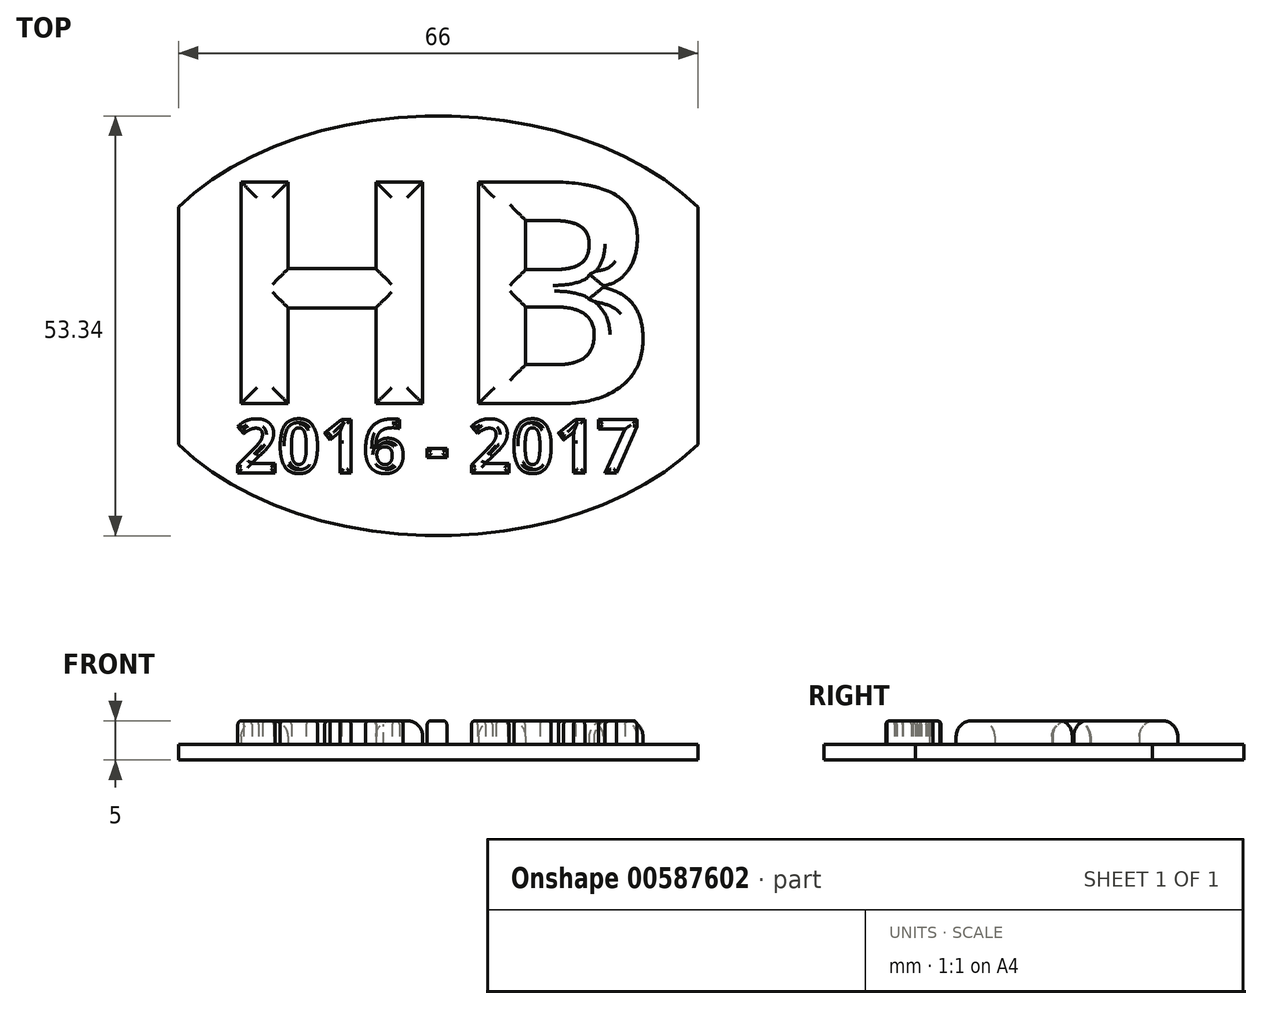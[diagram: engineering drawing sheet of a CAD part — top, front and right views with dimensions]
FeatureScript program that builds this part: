
annotation { "Feature Type Name" : "Feature", "Feature Type Description" : "" }
export const myFeature = defineFeature(function(context is Context, id is Id, definition is map)
    precondition{}
    {
        {
            var Q0;
            Q0=qCreatedBy(makeId("Top.planeOp"),FACE);
            var sketch = newSketch(context, id + "F0", { "sketchPlane" : qUnion([Q0])});
            skEllipse(sketch, "E0", {"center": v(0, 0) * mm, "majorRadius": 40 * mm, "minorRadius": 26.67 * mm, "majorAxis": v(1, 0)});
            skLineSegment(sketch, "E1", {"start": v(-33, 15.07) * mm, "end": v(-33, -15.07) * mm});
            skLineSegment(sketch, "E2", {"start": v(0, 26.67) * mm, "end": v(0, -26.67) * mm, "construction": true});
            skLineSegment(sketch, "E3.MirrorCS", {"start": v(33, 15.07) * mm, "end": v(33, -15.07) * mm});
            skText(sketch, "E4", { "text": "HB", "fontName": "OpenSans-Bold.ttf"});
            skText(sketch, "E5", { "text": "2016 - 2017\n", "fontName": "OpenSans-Bold.ttf"});
            const initialGuessF0  = {"E4": [-0.02857, -0.00987, 1, 0, 0.02839], "E5": [-0.02583, -0.01869, 1, 0, 0.00684]};
            skSetInitialGuess(sketch, initialGuessF0);
            skSolve(sketch);
        }
        {
            var Q0;
            {var subQ0=sQuery(id+"F0.wireOp",EDGE,"E1");Q0=makeQuery(id+"F0.imprint","IMPRINT",FACE,{"disambiguationData":[TD([[makeQuery(id+"F0.imprint","IMPRINT",EDGE,{"derivedFrom":subQ0}),1.0]])]});}
            var Q1;
            Q1=makeQuery(id+"F0.imprint","IMPRINT",FACE,{"disambiguationData":[TD([[makeQuery(id+"F0.imprint","IMPRINT",EDGE,{"derivedFrom":sQuery(id+"F0.wireOp",EDGE,"E4.sketch_text.stroke-31")}),1.0]])]});
            var Q2;
            Q2=makeQuery(id+"F0.imprint","IMPRINT",FACE,{"disambiguationData":[TD([[makeQuery(id+"F0.imprint","IMPRINT",EDGE,{"derivedFrom":sQuery(id+"F0.wireOp",EDGE,"E4.sketch_text.stroke-24")}),1.0]])]});
            var Q3;
            Q3=makeQuery(id+"F0.imprint","IMPRINT",FACE,{"disambiguationData":[TD([[makeQuery(id+"F0.imprint","IMPRINT",EDGE,{"derivedFrom":sQuery(id+"F0.wireOp",EDGE,"E5.sketch_text.stroke-111")}),1.0]])]});
            var Q4;
            Q4=makeQuery(id+"F0.imprint","IMPRINT",FACE,{"disambiguationData":[TD([[makeQuery(id+"F0.imprint","IMPRINT",EDGE,{"derivedFrom":sQuery(id+"F0.wireOp",EDGE,"E5.sketch_text.stroke-67")}),1.0]])]});
            var Q5;
            Q5=makeQuery(id+"F0.imprint","IMPRINT",FACE,{"disambiguationData":[TD([[makeQuery(id+"F0.imprint","IMPRINT",EDGE,{"derivedFrom":sQuery(id+"F0.wireOp",EDGE,"E5.sketch_text.stroke-32")}),1.0]])]});
            extrude(context, id + "F1", {"entities" : qUnion([Q0, Q1, Q2, Q3, Q4, Q5]), "depth" : 2 * mm, "offsetDistance" : 25 * mm});
        }
        {
            var Q0;
            Q0=makeQuery(id+"F0.imprint","IMPRINT",FACE,{"disambiguationData":[TD([[makeQuery(id+"F0.imprint","IMPRINT",EDGE,{"derivedFrom":sQuery(id+"F0.wireOp",EDGE,"E4.sketch_text.stroke-0")}),-1.0]])]});
            var Q1;
            Q1=makeQuery(id+"F0.imprint","IMPRINT",FACE,{"disambiguationData":[TD([[makeQuery(id+"F0.imprint","IMPRINT",EDGE,{"derivedFrom":sQuery(id+"F0.wireOp",EDGE,"E4.sketch_text.stroke-12")}),-1.0]])]});
            var Q2;
            Q2=makeQuery(id+"F0.imprint","IMPRINT",FACE,{"disambiguationData":[TD([[makeQuery(id+"F0.imprint","IMPRINT",EDGE,{"derivedFrom":sQuery(id+"F0.wireOp",EDGE,"E5.sketch_text.stroke-40")}),-1.0]])]});
            var Q3;
            Q3=makeQuery(id+"F0.imprint","IMPRINT",FACE,{"disambiguationData":[TD([[makeQuery(id+"F0.imprint","IMPRINT",EDGE,{"derivedFrom":sQuery(id+"F0.wireOp",EDGE,"E5.sketch_text.stroke-50")}),-1.0]])]});
            var Q4;
            Q4=makeQuery(id+"F0.imprint","IMPRINT",FACE,{"disambiguationData":[TD([[makeQuery(id+"F0.imprint","IMPRINT",EDGE,{"derivedFrom":sQuery(id+"F0.wireOp",EDGE,"E5.sketch_text.stroke-24")}),-1.0]])]});
            var Q5;
            Q5=makeQuery(id+"F0.imprint","IMPRINT",FACE,{"disambiguationData":[TD([[makeQuery(id+"F0.imprint","IMPRINT",EDGE,{"derivedFrom":sQuery(id+"F0.wireOp",EDGE,"E5.sketch_text.stroke-75")}),-1.0]])]});
            var Q6;
            Q6=makeQuery(id+"F0.imprint","IMPRINT",FACE,{"disambiguationData":[TD([[makeQuery(id+"F0.imprint","IMPRINT",EDGE,{"derivedFrom":sQuery(id+"F0.wireOp",EDGE,"E5.sketch_text.stroke-79")}),-1.0]])]});
            var Q7;
            Q7=makeQuery(id+"F0.imprint","IMPRINT",FACE,{"disambiguationData":[TD([[makeQuery(id+"F0.imprint","IMPRINT",EDGE,{"derivedFrom":sQuery(id+"F0.wireOp",EDGE,"E5.sketch_text.stroke-103")}),-1.0]])]});
            var Q8;
            Q8=makeQuery(id+"F0.imprint","IMPRINT",FACE,{"disambiguationData":[TD([[makeQuery(id+"F0.imprint","IMPRINT",EDGE,{"derivedFrom":sQuery(id+"F0.wireOp",EDGE,"E5.sketch_text.stroke-119")}),-1.0]])]});
            var Q9;
            Q9=makeQuery(id+"F0.imprint","IMPRINT",FACE,{"disambiguationData":[TD([[makeQuery(id+"F0.imprint","IMPRINT",EDGE,{"derivedFrom":sQuery(id+"F0.wireOp",EDGE,"E5.sketch_text.stroke-129")}),-1.0]])]});
            var Q10;
            Q10=makeQuery(id+"F0.imprint","IMPRINT",FACE,{"disambiguationData":[TD([[makeQuery(id+"F0.imprint","IMPRINT",EDGE,{"derivedFrom":sQuery(id+"F0.wireOp",EDGE,"E5.sketch_text.stroke-0")}),-1.0]])]});
            extrude(context, id + "F2", {"entities" : qUnion([Q0, Q1, Q2, Q3, Q4, Q5, Q6, Q7, Q8, Q9, Q10]), "operationType" : NewBodyOperationType.ADD, "depth" : 5 * mm, "offsetDistance" : 25 * mm});
        }
        {
            var Q0;
            Q0=makeQuery(id+"F2.opExtrude","CAP_FACE",FACE,{"disambiguationData":[OSD([sQuery(id+"F0.wireOp",EDGE,"E4.sketch_text.stroke-0"),sQuery(id+"F0.wireOp",EDGE,"E4.sketch_text.stroke-1"),sQuery(id+"F0.wireOp",EDGE,"E4.sketch_text.stroke-2"),sQuery(id+"F0.wireOp",EDGE,"E4.sketch_text.stroke-3"),sQuery(id+"F0.wireOp",EDGE,"E4.sketch_text.stroke-4"),sQuery(id+"F0.wireOp",EDGE,"E4.sketch_text.stroke-5"),sQuery(id+"F0.wireOp",EDGE,"E4.sketch_text.stroke-6"),sQuery(id+"F0.wireOp",EDGE,"E4.sketch_text.stroke-7"),sQuery(id+"F0.wireOp",EDGE,"E4.sketch_text.stroke-8"),sQuery(id+"F0.wireOp",EDGE,"E4.sketch_text.stroke-9"),sQuery(id+"F0.wireOp",EDGE,"E4.sketch_text.stroke-10"),sQuery(id+"F0.wireOp",EDGE,"E4.sketch_text.stroke-11")])],"isStart":false});
            var Q1;
            Q1=makeQuery(id+"F2.opExtrude","CAP_FACE",FACE,{"disambiguationData":[OSD([sQuery(id+"F0.wireOp",EDGE,"E4.sketch_text.stroke-12"),sQuery(id+"F0.wireOp",EDGE,"E4.sketch_text.stroke-13"),sQuery(id+"F0.wireOp",EDGE,"E4.sketch_text.stroke-14"),sQuery(id+"F0.wireOp",EDGE,"E4.sketch_text.stroke-15"),sQuery(id+"F0.wireOp",EDGE,"E4.sketch_text.stroke-16"),sQuery(id+"F0.wireOp",EDGE,"E4.sketch_text.stroke-17"),sQuery(id+"F0.wireOp",EDGE,"E4.sketch_text.stroke-18"),sQuery(id+"F0.wireOp",EDGE,"E4.sketch_text.stroke-19"),sQuery(id+"F0.wireOp",EDGE,"E4.sketch_text.stroke-20"),sQuery(id+"F0.wireOp",EDGE,"E4.sketch_text.stroke-21"),sQuery(id+"F0.wireOp",EDGE,"E4.sketch_text.stroke-22"),sQuery(id+"F0.wireOp",EDGE,"E4.sketch_text.stroke-23"),sQuery(id+"F0.wireOp",EDGE,"E4.sketch_text.stroke-24"),sQuery(id+"F0.wireOp",EDGE,"E4.sketch_text.stroke-25"),sQuery(id+"F0.wireOp",EDGE,"E4.sketch_text.stroke-26"),sQuery(id+"F0.wireOp",EDGE,"E4.sketch_text.stroke-27"),sQuery(id+"F0.wireOp",EDGE,"E4.sketch_text.stroke-28"),sQuery(id+"F0.wireOp",EDGE,"E4.sketch_text.stroke-29"),sQuery(id+"F0.wireOp",EDGE,"E4.sketch_text.stroke-30"),sQuery(id+"F0.wireOp",EDGE,"E4.sketch_text.stroke-31"),sQuery(id+"F0.wireOp",EDGE,"E4.sketch_text.stroke-32"),sQuery(id+"F0.wireOp",EDGE,"E4.sketch_text.stroke-33"),sQuery(id+"F0.wireOp",EDGE,"E4.sketch_text.stroke-34"),sQuery(id+"F0.wireOp",EDGE,"E4.sketch_text.stroke-35"),sQuery(id+"F0.wireOp",EDGE,"E4.sketch_text.stroke-36")])],"isStart":false});
            fillet(context, id + "F3", {"entities" : qUnion([Q0, Q1]), "radius" : 2 * mm, "tangentPropagation" : true, "allowEdgeOverflow" : false});
        }
        {
            var Q0;
            Q0=makeQuery(id+"F2.opExtrude","CAP_FACE",FACE,{"disambiguationData":[OSD([sQuery(id+"F0.wireOp",EDGE,"E5.sketch_text.stroke-0"),sQuery(id+"F0.wireOp",EDGE,"E5.sketch_text.stroke-1"),sQuery(id+"F0.wireOp",EDGE,"E5.sketch_text.stroke-2"),sQuery(id+"F0.wireOp",EDGE,"E5.sketch_text.stroke-3"),sQuery(id+"F0.wireOp",EDGE,"E5.sketch_text.stroke-4"),sQuery(id+"F0.wireOp",EDGE,"E5.sketch_text.stroke-5"),sQuery(id+"F0.wireOp",EDGE,"E5.sketch_text.stroke-6"),sQuery(id+"F0.wireOp",EDGE,"E5.sketch_text.stroke-7"),sQuery(id+"F0.wireOp",EDGE,"E5.sketch_text.stroke-8"),sQuery(id+"F0.wireOp",EDGE,"E5.sketch_text.stroke-9"),sQuery(id+"F0.wireOp",EDGE,"E5.sketch_text.stroke-10"),sQuery(id+"F0.wireOp",EDGE,"E5.sketch_text.stroke-11"),sQuery(id+"F0.wireOp",EDGE,"E5.sketch_text.stroke-12"),sQuery(id+"F0.wireOp",EDGE,"E5.sketch_text.stroke-13"),sQuery(id+"F0.wireOp",EDGE,"E5.sketch_text.stroke-14"),sQuery(id+"F0.wireOp",EDGE,"E5.sketch_text.stroke-15"),sQuery(id+"F0.wireOp",EDGE,"E5.sketch_text.stroke-16"),sQuery(id+"F0.wireOp",EDGE,"E5.sketch_text.stroke-17"),sQuery(id+"F0.wireOp",EDGE,"E5.sketch_text.stroke-18"),sQuery(id+"F0.wireOp",EDGE,"E5.sketch_text.stroke-19"),sQuery(id+"F0.wireOp",EDGE,"E5.sketch_text.stroke-20"),sQuery(id+"F0.wireOp",EDGE,"E5.sketch_text.stroke-21"),sQuery(id+"F0.wireOp",EDGE,"E5.sketch_text.stroke-22"),sQuery(id+"F0.wireOp",EDGE,"E5.sketch_text.stroke-23")])],"isStart":false});
            var Q1;
            Q1=makeQuery(id+"F2.opExtrude","CAP_FACE",FACE,{"disambiguationData":[OSD([sQuery(id+"F0.wireOp",EDGE,"E5.sketch_text.stroke-24"),sQuery(id+"F0.wireOp",EDGE,"E5.sketch_text.stroke-25"),sQuery(id+"F0.wireOp",EDGE,"E5.sketch_text.stroke-26"),sQuery(id+"F0.wireOp",EDGE,"E5.sketch_text.stroke-27"),sQuery(id+"F0.wireOp",EDGE,"E5.sketch_text.stroke-28"),sQuery(id+"F0.wireOp",EDGE,"E5.sketch_text.stroke-29"),sQuery(id+"F0.wireOp",EDGE,"E5.sketch_text.stroke-30"),sQuery(id+"F0.wireOp",EDGE,"E5.sketch_text.stroke-31"),sQuery(id+"F0.wireOp",EDGE,"E5.sketch_text.stroke-32"),sQuery(id+"F0.wireOp",EDGE,"E5.sketch_text.stroke-33"),sQuery(id+"F0.wireOp",EDGE,"E5.sketch_text.stroke-34"),sQuery(id+"F0.wireOp",EDGE,"E5.sketch_text.stroke-35"),sQuery(id+"F0.wireOp",EDGE,"E5.sketch_text.stroke-36"),sQuery(id+"F0.wireOp",EDGE,"E5.sketch_text.stroke-37"),sQuery(id+"F0.wireOp",EDGE,"E5.sketch_text.stroke-38"),sQuery(id+"F0.wireOp",EDGE,"E5.sketch_text.stroke-39")])],"isStart":false});
            var Q2;
            Q2=makeQuery(id+"F2.opExtrude","CAP_FACE",FACE,{"disambiguationData":[OSD([sQuery(id+"F0.wireOp",EDGE,"E5.sketch_text.stroke-40"),sQuery(id+"F0.wireOp",EDGE,"E5.sketch_text.stroke-41"),sQuery(id+"F0.wireOp",EDGE,"E5.sketch_text.stroke-42"),sQuery(id+"F0.wireOp",EDGE,"E5.sketch_text.stroke-43"),sQuery(id+"F0.wireOp",EDGE,"E5.sketch_text.stroke-44"),sQuery(id+"F0.wireOp",EDGE,"E5.sketch_text.stroke-45"),sQuery(id+"F0.wireOp",EDGE,"E5.sketch_text.stroke-46"),sQuery(id+"F0.wireOp",EDGE,"E5.sketch_text.stroke-47"),sQuery(id+"F0.wireOp",EDGE,"E5.sketch_text.stroke-48"),sQuery(id+"F0.wireOp",EDGE,"E5.sketch_text.stroke-49")])],"isStart":false});
            var Q3;
            Q3=makeQuery(id+"F2.opExtrude","CAP_FACE",FACE,{"disambiguationData":[OSD([sQuery(id+"F0.wireOp",EDGE,"E5.sketch_text.stroke-50"),sQuery(id+"F0.wireOp",EDGE,"E5.sketch_text.stroke-51"),sQuery(id+"F0.wireOp",EDGE,"E5.sketch_text.stroke-52"),sQuery(id+"F0.wireOp",EDGE,"E5.sketch_text.stroke-53"),sQuery(id+"F0.wireOp",EDGE,"E5.sketch_text.stroke-54"),sQuery(id+"F0.wireOp",EDGE,"E5.sketch_text.stroke-55"),sQuery(id+"F0.wireOp",EDGE,"E5.sketch_text.stroke-56"),sQuery(id+"F0.wireOp",EDGE,"E5.sketch_text.stroke-57"),sQuery(id+"F0.wireOp",EDGE,"E5.sketch_text.stroke-58"),sQuery(id+"F0.wireOp",EDGE,"E5.sketch_text.stroke-59"),sQuery(id+"F0.wireOp",EDGE,"E5.sketch_text.stroke-60"),sQuery(id+"F0.wireOp",EDGE,"E5.sketch_text.stroke-61"),sQuery(id+"F0.wireOp",EDGE,"E5.sketch_text.stroke-62"),sQuery(id+"F0.wireOp",EDGE,"E5.sketch_text.stroke-63"),sQuery(id+"F0.wireOp",EDGE,"E5.sketch_text.stroke-64"),sQuery(id+"F0.wireOp",EDGE,"E5.sketch_text.stroke-65"),sQuery(id+"F0.wireOp",EDGE,"E5.sketch_text.stroke-66"),sQuery(id+"F0.wireOp",EDGE,"E5.sketch_text.stroke-67"),sQuery(id+"F0.wireOp",EDGE,"E5.sketch_text.stroke-68"),sQuery(id+"F0.wireOp",EDGE,"E5.sketch_text.stroke-69"),sQuery(id+"F0.wireOp",EDGE,"E5.sketch_text.stroke-70"),sQuery(id+"F0.wireOp",EDGE,"E5.sketch_text.stroke-71"),sQuery(id+"F0.wireOp",EDGE,"E5.sketch_text.stroke-72"),sQuery(id+"F0.wireOp",EDGE,"E5.sketch_text.stroke-73"),sQuery(id+"F0.wireOp",EDGE,"E5.sketch_text.stroke-74")])],"isStart":false});
            var Q4;
            Q4=makeQuery(id+"F2.opExtrude","CAP_FACE",FACE,{"disambiguationData":[OSD([sQuery(id+"F0.wireOp",EDGE,"E5.sketch_text.stroke-75"),sQuery(id+"F0.wireOp",EDGE,"E5.sketch_text.stroke-76"),sQuery(id+"F0.wireOp",EDGE,"E5.sketch_text.stroke-77"),sQuery(id+"F0.wireOp",EDGE,"E5.sketch_text.stroke-78")])],"isStart":false});
            var Q5;
            Q5=makeQuery(id+"F2.opExtrude","CAP_FACE",FACE,{"disambiguationData":[OSD([sQuery(id+"F0.wireOp",EDGE,"E5.sketch_text.stroke-79"),sQuery(id+"F0.wireOp",EDGE,"E5.sketch_text.stroke-80"),sQuery(id+"F0.wireOp",EDGE,"E5.sketch_text.stroke-81"),sQuery(id+"F0.wireOp",EDGE,"E5.sketch_text.stroke-82"),sQuery(id+"F0.wireOp",EDGE,"E5.sketch_text.stroke-83"),sQuery(id+"F0.wireOp",EDGE,"E5.sketch_text.stroke-84"),sQuery(id+"F0.wireOp",EDGE,"E5.sketch_text.stroke-85"),sQuery(id+"F0.wireOp",EDGE,"E5.sketch_text.stroke-86"),sQuery(id+"F0.wireOp",EDGE,"E5.sketch_text.stroke-87"),sQuery(id+"F0.wireOp",EDGE,"E5.sketch_text.stroke-88"),sQuery(id+"F0.wireOp",EDGE,"E5.sketch_text.stroke-89"),sQuery(id+"F0.wireOp",EDGE,"E5.sketch_text.stroke-90"),sQuery(id+"F0.wireOp",EDGE,"E5.sketch_text.stroke-91"),sQuery(id+"F0.wireOp",EDGE,"E5.sketch_text.stroke-92"),sQuery(id+"F0.wireOp",EDGE,"E5.sketch_text.stroke-93"),sQuery(id+"F0.wireOp",EDGE,"E5.sketch_text.stroke-94"),sQuery(id+"F0.wireOp",EDGE,"E5.sketch_text.stroke-95"),sQuery(id+"F0.wireOp",EDGE,"E5.sketch_text.stroke-96"),sQuery(id+"F0.wireOp",EDGE,"E5.sketch_text.stroke-97"),sQuery(id+"F0.wireOp",EDGE,"E5.sketch_text.stroke-98"),sQuery(id+"F0.wireOp",EDGE,"E5.sketch_text.stroke-99"),sQuery(id+"F0.wireOp",EDGE,"E5.sketch_text.stroke-100"),sQuery(id+"F0.wireOp",EDGE,"E5.sketch_text.stroke-101"),sQuery(id+"F0.wireOp",EDGE,"E5.sketch_text.stroke-102")])],"isStart":false});
            var Q6;
            Q6=makeQuery(id+"F2.opExtrude","CAP_FACE",FACE,{"disambiguationData":[OSD([sQuery(id+"F0.wireOp",EDGE,"E5.sketch_text.stroke-103"),sQuery(id+"F0.wireOp",EDGE,"E5.sketch_text.stroke-104"),sQuery(id+"F0.wireOp",EDGE,"E5.sketch_text.stroke-105"),sQuery(id+"F0.wireOp",EDGE,"E5.sketch_text.stroke-106"),sQuery(id+"F0.wireOp",EDGE,"E5.sketch_text.stroke-107"),sQuery(id+"F0.wireOp",EDGE,"E5.sketch_text.stroke-108"),sQuery(id+"F0.wireOp",EDGE,"E5.sketch_text.stroke-109"),sQuery(id+"F0.wireOp",EDGE,"E5.sketch_text.stroke-110"),sQuery(id+"F0.wireOp",EDGE,"E5.sketch_text.stroke-111"),sQuery(id+"F0.wireOp",EDGE,"E5.sketch_text.stroke-112"),sQuery(id+"F0.wireOp",EDGE,"E5.sketch_text.stroke-113"),sQuery(id+"F0.wireOp",EDGE,"E5.sketch_text.stroke-114"),sQuery(id+"F0.wireOp",EDGE,"E5.sketch_text.stroke-115"),sQuery(id+"F0.wireOp",EDGE,"E5.sketch_text.stroke-116"),sQuery(id+"F0.wireOp",EDGE,"E5.sketch_text.stroke-117"),sQuery(id+"F0.wireOp",EDGE,"E5.sketch_text.stroke-118")])],"isStart":false});
            var Q7;
            Q7=makeQuery(id+"F2.opExtrude","CAP_FACE",FACE,{"disambiguationData":[OSD([sQuery(id+"F0.wireOp",EDGE,"E5.sketch_text.stroke-119"),sQuery(id+"F0.wireOp",EDGE,"E5.sketch_text.stroke-120"),sQuery(id+"F0.wireOp",EDGE,"E5.sketch_text.stroke-121"),sQuery(id+"F0.wireOp",EDGE,"E5.sketch_text.stroke-122"),sQuery(id+"F0.wireOp",EDGE,"E5.sketch_text.stroke-123"),sQuery(id+"F0.wireOp",EDGE,"E5.sketch_text.stroke-124"),sQuery(id+"F0.wireOp",EDGE,"E5.sketch_text.stroke-125"),sQuery(id+"F0.wireOp",EDGE,"E5.sketch_text.stroke-126"),sQuery(id+"F0.wireOp",EDGE,"E5.sketch_text.stroke-127"),sQuery(id+"F0.wireOp",EDGE,"E5.sketch_text.stroke-128")])],"isStart":false});
            var Q8;
            Q8=makeQuery(id+"F2.opExtrude","CAP_FACE",FACE,{"disambiguationData":[OSD([sQuery(id+"F0.wireOp",EDGE,"E5.sketch_text.stroke-129"),sQuery(id+"F0.wireOp",EDGE,"E5.sketch_text.stroke-130"),sQuery(id+"F0.wireOp",EDGE,"E5.sketch_text.stroke-131"),sQuery(id+"F0.wireOp",EDGE,"E5.sketch_text.stroke-132"),sQuery(id+"F0.wireOp",EDGE,"E5.sketch_text.stroke-133"),sQuery(id+"F0.wireOp",EDGE,"E5.sketch_text.stroke-134"),sQuery(id+"F0.wireOp",EDGE,"E5.sketch_text.stroke-135")])],"isStart":false});
            fillet(context, id + "F4", {"entities" : qUnion([Q0, Q1, Q2, Q3, Q4, Q5, Q6, Q7, Q8]), "radius" : .5 * mm, "tangentPropagation" : true, "allowEdgeOverflow" : false});
        }
    });
